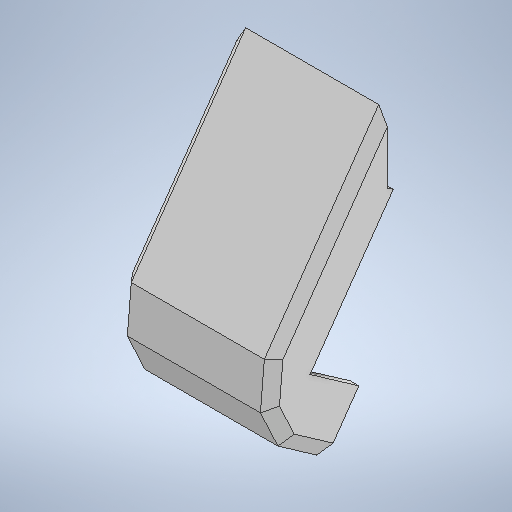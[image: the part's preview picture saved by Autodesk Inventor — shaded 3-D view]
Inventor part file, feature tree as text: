
AUTODESK INVENTOR PART (.ipt)
format: ipt  version: 2025.2 (Build 292293000, 293)  size: 1,209,344 bytes
history: native  units: in
note: dims shown in document units (in); Inventor stores cm internally (conversion verified against a paired STEP export)
features: sketch x43, extrude x39, projected_geometry x9, plane x8, move_body x1, chamfer x1, fillet x1, hole x1
ambient origin geometry x8: Origin, YZ Plane, XZ Plane, XY Plane, X Axis, Y Axis, Z Axis, Center Point
bodies: Solid1 (feature_tree)
feature tree (103):
  extrude  "Extrusion1"  Depth=0.1969in TaperAngle=0.0deg
  move_body  "Move Body1"
  plane  "Work Plane1"
  sketch  "Sketch5"  dims[d5=1.7717in d6=1.7717in d7=1.7717in d8=1.7717in d9=0.8108in d10=90.0deg d11=0.0787in d12=0.3701in d13=0.4252in d14=0.1362in d15=-0.0984in d16=-0.0591in d17=0.0in]
  plane  "Work Plane2"
  extrude  "Extrusion4"  TaperAngle=0.0deg  [1 undecoded]
  extrude  "Extrusion6"  Depth=0.2405in
  extrude  "Extrusion8"  Depth=2.5591in TaperAngle=0.0deg
  chamfer  "Chamfer1"  [1 undecoded]
  extrude  "Extrusion11"  Depth=0.2362in
  plane  "Work Plane3"
  plane  "Work Plane7"
  extrude  "Extrusion22"  Depth=0.1969in TaperAngle=0.0deg
  extrude  "Extrusion25"  Depth=0.5027in
  extrude  "Extrusion26"  Depth=0.5027in
  sketch  "Sketch33"  dims[d96=0.2362in d97=0.0in d100=3.6403in]
  extrude  "Extrusion27"  Depth=0.2362in TaperAngle=0.0deg
  extrude  "Extrusion28"  Depth=3.6403in
  sketch  "Sketch36"  dims[d123=0.9331in d124=0.9712in d125=0.0in]
  extrude  "Extrusion29"  Depth=1.9685in
  extrude  "Extrusion30"  Depth=0.1575in
  extrude  "Extrusion31"  Depth=0.9712in TaperAngle=0.0deg
  sketch  "Sketch39"  dims[d138=0.4331in d139=0.1181in d140=0.0in]
  extrude  "Extrusion32"  Depth=11.3469in TaperAngle=0.0deg
  fillet  "Fillet1"  Radius=11.3469in
  extrude  "Extrusion33"  Depth=0.4331in
  extrude  "Extrusion34"  Depth=0.1181in TaperAngle=0.0deg
  extrude  "Extrusion35"  Depth=0.0787in
  plane  "Work Plane8"
  sketch  "Sketch45"  dims[d160=0.1181in d161=0.0in d162=0.1969in d163=0.0in d164=0.1181in d165=0.0in]
  extrude  "Extrusion37"  Depth=0.2756in
  extrude  "Extrusion38"  Depth=0.1181in TaperAngle=0.0deg
  extrude  "Extrusion40"  Depth=0.5906in
  extrude  "Extrusion41"  Depth=0.1181in TaperAngle=0.0deg
  extrude  "Extrusion43"  Depth=4.7244in TaperAngle=0.0deg
  extrude  "Extrusion44"  Depth=0.7313in TaperAngle=0.0deg
  extrude  "Extrusion46"  TaperAngle=0.0deg  [1 undecoded]
  extrude  "Extrusion48"  Depth=1.1024in
  extrude  "Extrusion50"  Depth=0.0394in TaperAngle=0.0deg
  extrude  "Extrusion51"  Depth=5.8937in TaperAngle=0.0deg
  extrude  "Extrusion53"  Depth=0.5917in TaperAngle=0.0deg
  plane  "Work Plane9"
  extrude  "Extrusion55"  TaperAngle=0.0deg  [1 undecoded]
  extrude  "Extrusion56"  Depth=1.1811in TaperAngle=0.0deg
  plane  "Work Plane10"
  extrude  "Extrusion57"  TaperAngle=0.0deg  [1 undecoded]
  plane  "Work Plane11"
  extrude  "Extrusion58"  TaperAngle=0.0deg  [1 undecoded]
  extrude  "Extrusion59"  Depth=0.2362in TaperAngle=0.0deg
  extrude  "Extrusion60"  Depth=0.5118in TaperAngle=0.0deg
  extrude  "Extrusion61"  Depth=0.1969in
  extrude  "Extrusion62"  TaperAngle=60.0deg  [1 undecoded]
  extrude  "Extrusion63"  Depth=0.0394in TaperAngle=0.0deg
  extrude  "Extrusion65"  Depth=0.0344in
  extrude  "Extrusion66"  Depth=0.0344in
  sketch  "Sketch1"  dims[d1=0.5512in d2=0.1969in d3=0.0in]
  sketch  "Sketch6"  dims[d18=0.2749in d24=0.2405in]
  sketch  "Sketch8"  dims[d25=2.7559in d26=0.0in d29=2.5591in d30=0.0in d36=0.0in d37=0.0in]
  sketch  "Sketch12"  dims[d42=0.2362in d43=0.2362in]
  sketch  "Sketch15"  dims[d52=0.2362in d53=0.0787in d54=45.0deg d55=0.1969in d56=0.0in]
  sketch  "Sketch28"  dims[d76=0.5027in d77=0.5027in]
  sketch  "Sketch31"  dims[d78=0.5027in d79=0.5027in]
  sketch  "Sketch32"  dims[d83=0.0in d84=0.0in d94=0.2362in d95=0.0in]
  sketch  "Sketch34"  dims[d101=2.7717in d112=1.9685in]
  sketch  "Sketch35"  dims[d113=0.6299in d114=0.0in d115=0.1575in d117=0.1575in d121=1.9685in d122=0.7874in]
  sketch  "Sketch37"  dims[d126=0.5906in d127=0.0in d128=11.3469in d129=0.0in d130=11.3469in d131=0.0in]
  sketch  "Sketch38"  dims[d136=0.4331in d137=0.4331in]
  sketch  "Sketch40"  dims[d141=0.6299in d142=0.0787in]
  sketch  "Sketch41"  dims[d147=0.2756in d149=0.2756in]
  sketch  "Sketch42"  dims[d150=0.0in d151=0.0in d154=0.1181in d155=0.0in]
  sketch  "Sketch44"  dims[d156=0.1181in d157=0.0in d158=0.5906in]
  projected_geometry  "Projected Loop2"
  projected_geometry  "Projected Loop3"
  projected_geometry  "Projected Loop5"
  sketch  "Sketch47"  dims[d168=0.5906in d169=0.0in d170=4.7244in d171=0.0in]
  sketch  "Sketch49"  dims[d174=0.0in d175=0.0in d176=0.7313in d177=0.0in]
  sketch  "Sketch50"  dims[d186=0.0in d187=0.0in d188=0.0in d189=0.0in]
  sketch  "Sketch52"  dims[d194=0.0in d195=0.0in d196=1.1024in]
  sketch  "Sketch53"  dims[d197=0.5906in d200=0.0394in d201=0.0in]
  sketch  "Sketch56"  dims[d218=0.0in d219=0.0in d220=5.8937in d221=0.0in]
  sketch  "Sketch59"  dims[d233=0.9963in d234=0.5917in d235=0.0in]
  sketch  "Sketch60"  dims[d241=1.378in d242=0.0in d243=0.0in d244=0.0in]
  sketch  "Sketch61"  dims[d245=120.0deg d246=1.1811in d247=0.0in]
  sketch  "Sketch63"  dims[d248=120.0deg d249=0.0in d250=0.0in]
  projected_geometry  "Projected Loop8"
  sketch  "Sketch65"  dims[d251=0.7874in d252=0.0in d253=0.0in d254=0.0in]
  projected_geometry  "Projected Loop9"
  sketch  "Sketch67"  dims[d255=0.2362in d256=0.0in d257=0.2362in d258=0.0in]
  sketch  "Sketch68"  dims[d259=0.2362in d260=0.5118in d261=0.0in]
  projected_geometry  "Projected Loop10"
  sketch  "Sketch69"  dims[d266=0.1378in d268=0.1969in]
  sketch  "Sketch70"  dims[d269=0.1378in d270=60.0deg]
  projected_geometry  "Projected Loop11"
  sketch  "Sketch71"  dims[d271=3.9671in d272=0.0in d273=0.0394in d274=0.0in]
  projected_geometry  "Projected Loop12"
  sketch  "Sketch72"  dims[d38=0.0197in d39=0.0344in]
  sketch  "Sketch73"  dims[d57=0.0197in d58=0.0344in]
  sketch  "Sketch74"  dims[d59=0.0197in d60=0.0344in]
  projected_geometry  "Projected Loop13"
  sketch  "Sketch76"  dims[d81=0.0197in]
  sketch  "Sketch77"  dims[d82=0.0344in d159=0.0344in d178=0.0in d179=0.0in d180=0.0in d181=0.0in d202=0.0197in d203=0.0344in d222=0.0197in d223=0.0344in]
  sketch  "Sketch2"  dims[d4=0.315in]
  hole  "Hole1"  [1 undecoded]
note: 8 required parameter values undecoded (feature->parameter linkage not recoverable at this tier; creation-order binding heuristic only, values carry confidence <= 0.55)
